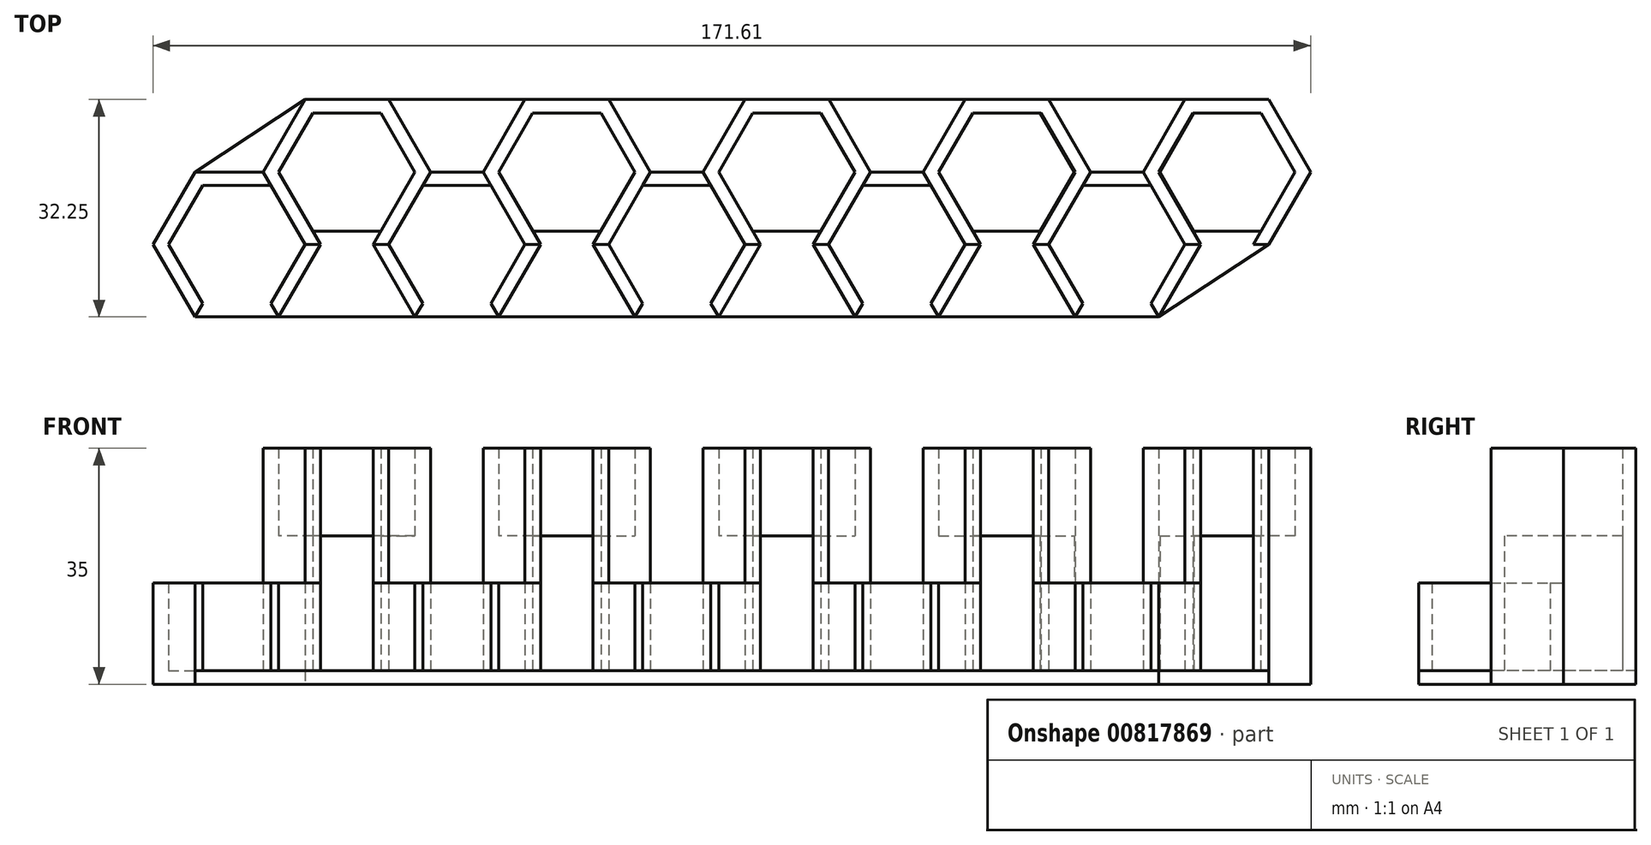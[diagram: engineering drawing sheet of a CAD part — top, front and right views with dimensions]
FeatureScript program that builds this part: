
annotation { "Feature Type Name" : "Feature", "Feature Type Description" : "" }
export const myFeature = defineFeature(function(context is Context, id is Id, definition is map)
    precondition{}
    {
        {
            var Q0;
            Q0=qCreatedBy(makeId("Top.planeOp"),FACE);
            var sketch = newSketch(context, id + "F0", { "sketchPlane" : qUnion([Q0])});
            skLineSegment(sketch, "E0.0", {"start": v(-33.3, -2) * mm, "end": v(-28.26, -10.75) * mm});
            skLineSegment(sketch, "E0.1", {"start": v(-28.26, -10.75) * mm, "end": v(-33.3, -19.5) * mm});
            skLineSegment(sketch, "E0.3", {"start": v(-43.41, -19.5) * mm, "end": v(-48.46, -10.75) * mm});
            skLineSegment(sketch, "E0.4", {"start": v(-48.46, -10.75) * mm, "end": v(-43.41, -2) * mm});
            skLineSegment(sketch, "E0.5", {"start": v(-43.41, -2) * mm, "end": v(-33.3, -2) * mm});
            skPoint(sketch, "E0.0.midPoint", {"position": v(-30.78, -6.38) * mm});
            skLineSegment(sketch, "E1.0", {"start": v(-32.15, 0) * mm, "end": v(-25.95, -10.75) * mm});
            skLineSegment(sketch, "E1.1", {"start": v(-25.95, -10.75) * mm, "end": v(-32.15, -21.5) * mm});
            skLineSegment(sketch, "E1.3", {"start": v(-44.57, -21.5) * mm, "end": v(-50.77, -10.75) * mm});
            skLineSegment(sketch, "E1.4", {"start": v(-50.77, -10.75) * mm, "end": v(-44.57, 0) * mm});
            skLineSegment(sketch, "E1.5", {"start": v(-42.26, 0) * mm, "end": v(-34.46, 0) * mm});
            skPoint(sketch, "E1.0.midPoint", {"position": v(-29.05, -5.38) * mm});
            skLineSegment(sketch, "E2.2", {"start": v(-27.1, -8.75) * mm, "end": v(-32.15, 0) * mm});
            skLineSegment(sketch, "E2.3", {"start": v(-32.15, 0) * mm, "end": v(-27.1, 8.75) * mm});
            skLineSegment(sketch, "E2.4", {"start": v(-27.1, 8.75) * mm, "end": v(-22.05, 8.75) * mm});
            skPoint(sketch, "E2.0.midPoint", {"position": v(-14.47, -4.38) * mm});
            skLineSegment(sketch, "E3.3", {"start": v(-28.26, -10.75) * mm, "end": v(-33.3, -2) * mm});
            skLineSegment(sketch, "E3.4", {"start": v(-34.46, 0) * mm, "end": v(-28.26, 10.75) * mm});
            skLineSegment(sketch, "E3.5", {"start": v(-28.26, 10.75) * mm, "end": v(-22.05, 10.75) * mm});
            skPoint(sketch, "E3.0.midPoint", {"position": v(-12.74, 5.37) * mm});
            skLineSegment(sketch, "E4", {"start": v(-44.57, -21.5) * mm, "end": v(-43.41, -19.5) * mm});
            skLineSegment(sketch, "E5", {"start": v(-33.3, -19.5) * mm, "end": v(-32.15, -21.5) * mm});
            skLineSegment(sketch, "E6", {"start": v(-22.05, 10.75) * mm, "end": v(-22.05, -27.83) * mm, "construction": true});
            skLineSegment(sketch, "E7", {"start": v(-22.05, -27.83) * mm, "end": v(-22.05, 12.83) * mm, "construction": true});
            skPoint(sketch, "E8.orphan", {"position": v(-15.84, 10.75) * mm});
            skPoint(sketch, "E3.1.start.orphan", {"position": v(-9.64, 0) * mm});
            skPoint(sketch, "E9.orphan", {"position": v(-11.95, 0) * mm});
            skPoint(sketch, "E10.end.orphan", {"position": v(-17, -8.75) * mm});
            skLineSegment(sketch, "E11.MirrorCS", {"start": v(-17, 8.75) * mm, "end": v(-22.05, 8.75) * mm});
            skLineSegment(sketch, "E12.MirrorCS", {"start": v(-15.84, 10.75) * mm, "end": v(-22.05, 10.75) * mm});
            skLineSegment(sketch, "E13.MirrorCS", {"start": v(-9.64, 0) * mm, "end": v(-15.84, 10.75) * mm});
            skLineSegment(sketch, "E14.MirrorCS", {"start": v(-11.95, 0) * mm, "end": v(-17, 8.75) * mm});
            skLineSegment(sketch, "E15.MirrorCS", {"start": v(-17, -8.75) * mm, "end": v(-11.95, 0) * mm});
            skLineSegment(sketch, "E16.MirrorCS", {"start": v(-14.47, -4.38) * mm, "end": v(-18.15, -10.75) * mm});
            skLineSegment(sketch, "E17.MirrorCS", {"start": v(-10.8, -2) * mm, "end": v(-15.84, -10.75) * mm});
            skLineSegment(sketch, "E18.1.0.0", {"start": v(-77.19, -21.5) * mm, "end": v(-83.4, -10.75) * mm});
            skLineSegment(sketch, "E18.1.0.1", {"start": v(-77.19, -21.5) * mm, "end": v(-76.03, -19.5) * mm});
            skLineSegment(sketch, "E18.1.0.2", {"start": v(-76.03, -19.5) * mm, "end": v(-81.08, -10.75) * mm});
            skLineSegment(sketch, "E18.1.0.3", {"start": v(-83.4, -10.75) * mm, "end": v(-77.19, 0) * mm});
            skLineSegment(sketch, "E18.1.0.4", {"start": v(-81.08, -10.75) * mm, "end": v(-76.03, -2) * mm});
            skLineSegment(sketch, "E18.1.0.5", {"start": v(-74.88, 0) * mm, "end": v(-67.08, 0) * mm});
            skLineSegment(sketch, "E18.1.0.6", {"start": v(-76.03, -2) * mm, "end": v(-65.93, -2) * mm});
            skLineSegment(sketch, "E18.1.0.7", {"start": v(-65.93, -2) * mm, "end": v(-60.88, -10.75) * mm});
            skLineSegment(sketch, "E18.1.0.8", {"start": v(-60.88, -10.75) * mm, "end": v(-65.93, -19.5) * mm});
            skLineSegment(sketch, "E18.1.0.9", {"start": v(-65.93, -19.5) * mm, "end": v(-64.77, -21.5) * mm});
            skLineSegment(sketch, "E18.1.0.10", {"start": v(-58.57, -10.75) * mm, "end": v(-64.77, -21.5) * mm});
            skLineSegment(sketch, "E18.1.0.11", {"start": v(-64.77, 0) * mm, "end": v(-58.57, -10.75) * mm});
            skLineSegment(sketch, "E18.1.0.12", {"start": v(-67.08, 0) * mm, "end": v(-60.88, 10.75) * mm});
            skLineSegment(sketch, "E18.1.0.13", {"start": v(-64.77, 0) * mm, "end": v(-59.72, 8.75) * mm});
            skLineSegment(sketch, "E18.1.0.14", {"start": v(-60.88, 10.75) * mm, "end": v(-54.67, 10.75) * mm});
            skLineSegment(sketch, "E18.1.0.15", {"start": v(-59.72, 8.75) * mm, "end": v(-54.67, 8.75) * mm});
            skLineSegment(sketch, "E18.1.0.16", {"start": v(-49.62, 8.75) * mm, "end": v(-54.67, 8.75) * mm});
            skLineSegment(sketch, "E18.1.0.17", {"start": v(-48.46, 10.75) * mm, "end": v(-54.67, 10.75) * mm});
            skLineSegment(sketch, "E18.1.0.18", {"start": v(-42.26, 0) * mm, "end": v(-48.46, 10.75) * mm});
            skLineSegment(sketch, "E18.1.0.19", {"start": v(-44.57, 0) * mm, "end": v(-49.62, 8.75) * mm});
            skLineSegment(sketch, "E18.2.0.0", {"start": v(-109.8, -21.5) * mm, "end": v(-116.01, -10.75) * mm});
            skLineSegment(sketch, "E18.2.0.1", {"start": v(-109.8, -21.5) * mm, "end": v(-108.65, -19.5) * mm});
            skLineSegment(sketch, "E18.2.0.2", {"start": v(-108.65, -19.5) * mm, "end": v(-113.7, -10.75) * mm});
            skLineSegment(sketch, "E18.2.0.3", {"start": v(-116.01, -10.75) * mm, "end": v(-109.8, 0) * mm});
            skLineSegment(sketch, "E18.2.0.4", {"start": v(-113.7, -10.75) * mm, "end": v(-108.65, -2) * mm});
            skLineSegment(sketch, "E18.2.0.5", {"start": v(-107.5, 0) * mm, "end": v(-99.7, 0) * mm});
            skLineSegment(sketch, "E18.2.0.6", {"start": v(-108.65, -2) * mm, "end": v(-98.55, -2) * mm});
            skLineSegment(sketch, "E18.2.0.7", {"start": v(-98.55, -2) * mm, "end": v(-93.5, -10.75) * mm});
            skLineSegment(sketch, "E18.2.0.8", {"start": v(-93.5, -10.75) * mm, "end": v(-98.55, -19.5) * mm});
            skLineSegment(sketch, "E18.2.0.9", {"start": v(-98.55, -19.5) * mm, "end": v(-97.4, -21.5) * mm});
            skLineSegment(sketch, "E18.2.0.10", {"start": v(-91.19, -10.75) * mm, "end": v(-97.4, -21.5) * mm});
            skLineSegment(sketch, "E18.2.0.11", {"start": v(-97.4, 0) * mm, "end": v(-91.19, -10.75) * mm});
            skLineSegment(sketch, "E18.2.0.12", {"start": v(-99.7, 0) * mm, "end": v(-93.5, 10.75) * mm});
            skLineSegment(sketch, "E18.2.0.13", {"start": v(-97.4, 0) * mm, "end": v(-92.34, 8.75) * mm});
            skLineSegment(sketch, "E18.2.0.14", {"start": v(-93.5, 10.75) * mm, "end": v(-87.29, 10.75) * mm});
            skLineSegment(sketch, "E18.2.0.15", {"start": v(-92.34, 8.75) * mm, "end": v(-87.29, 8.75) * mm});
            skLineSegment(sketch, "E18.2.0.16", {"start": v(-82.24, 8.75) * mm, "end": v(-87.29, 8.75) * mm});
            skLineSegment(sketch, "E18.2.0.17", {"start": v(-81.08, 10.75) * mm, "end": v(-87.29, 10.75) * mm});
            skLineSegment(sketch, "E18.2.0.18", {"start": v(-74.88, 0) * mm, "end": v(-81.08, 10.75) * mm});
            skLineSegment(sketch, "E18.2.0.19", {"start": v(-77.19, 0) * mm, "end": v(-82.24, 8.75) * mm});
            skLineSegment(sketch, "E18.3.0.0", {"start": v(-142.43, -21.5) * mm, "end": v(-148.63, -10.75) * mm});
            skLineSegment(sketch, "E18.3.0.1", {"start": v(-142.43, -21.5) * mm, "end": v(-141.27, -19.5) * mm});
            skLineSegment(sketch, "E18.3.0.2", {"start": v(-141.27, -19.5) * mm, "end": v(-146.32, -10.75) * mm});
            skLineSegment(sketch, "E18.3.0.3", {"start": v(-148.63, -10.75) * mm, "end": v(-142.43, 0) * mm});
            skLineSegment(sketch, "E18.3.0.4", {"start": v(-146.32, -10.75) * mm, "end": v(-141.27, -2) * mm});
            skLineSegment(sketch, "E18.3.0.5", {"start": v(-140.12, 0) * mm, "end": v(-132.32, 0) * mm});
            skLineSegment(sketch, "E18.3.0.6", {"start": v(-141.27, -2) * mm, "end": v(-131.17, -2) * mm});
            skLineSegment(sketch, "E18.3.0.7", {"start": v(-131.17, -2) * mm, "end": v(-126.12, -10.75) * mm});
            skLineSegment(sketch, "E18.3.0.8", {"start": v(-126.12, -10.75) * mm, "end": v(-131.17, -19.5) * mm});
            skLineSegment(sketch, "E18.3.0.9", {"start": v(-131.17, -19.5) * mm, "end": v(-130.01, -21.5) * mm});
            skLineSegment(sketch, "E18.3.0.10", {"start": v(-123.8, -10.75) * mm, "end": v(-130.01, -21.5) * mm});
            skLineSegment(sketch, "E18.3.0.11", {"start": v(-130.01, 0) * mm, "end": v(-123.8, -10.75) * mm});
            skLineSegment(sketch, "E18.3.0.12", {"start": v(-132.32, 0) * mm, "end": v(-126.12, 10.75) * mm});
            skLineSegment(sketch, "E18.3.0.13", {"start": v(-130.01, 0) * mm, "end": v(-124.96, 8.75) * mm});
            skLineSegment(sketch, "E18.3.0.14", {"start": v(-126.12, 10.75) * mm, "end": v(-119.9, 10.75) * mm});
            skLineSegment(sketch, "E18.3.0.15", {"start": v(-124.96, 8.75) * mm, "end": v(-119.9, 8.75) * mm});
            skLineSegment(sketch, "E18.3.0.16", {"start": v(-114.86, 8.75) * mm, "end": v(-119.9, 8.75) * mm});
            skLineSegment(sketch, "E18.3.0.17", {"start": v(-113.7, 10.75) * mm, "end": v(-119.9, 10.75) * mm});
            skLineSegment(sketch, "E18.3.0.18", {"start": v(-107.5, 0) * mm, "end": v(-113.7, 10.75) * mm});
            skLineSegment(sketch, "E18.3.0.19", {"start": v(-109.8, 0) * mm, "end": v(-114.86, 8.75) * mm});
            skLineSegment(sketch, "E18.4.0.0", {"start": v(-175.05, -21.5) * mm, "end": v(-181.25, -10.75) * mm});
            skLineSegment(sketch, "E18.4.0.1", {"start": v(-175.05, -21.5) * mm, "end": v(-173.9, -19.5) * mm});
            skLineSegment(sketch, "E18.4.0.2", {"start": v(-173.9, -19.5) * mm, "end": v(-178.94, -10.75) * mm});
            skLineSegment(sketch, "E18.4.0.3", {"start": v(-181.25, -10.75) * mm, "end": v(-175.05, 0) * mm});
            skLineSegment(sketch, "E18.4.0.4", {"start": v(-178.94, -10.75) * mm, "end": v(-173.9, -2) * mm});
            skLineSegment(sketch, "E18.4.0.5", {"start": v(-175.05, 0) * mm, "end": v(-164.94, 0) * mm});
            skLineSegment(sketch, "E18.4.0.6", {"start": v(-173.9, -2) * mm, "end": v(-163.79, -2) * mm});
            skLineSegment(sketch, "E18.4.0.7", {"start": v(-163.79, -2) * mm, "end": v(-158.74, -10.75) * mm});
            skLineSegment(sketch, "E18.4.0.8", {"start": v(-158.74, -10.75) * mm, "end": v(-163.79, -19.5) * mm});
            skLineSegment(sketch, "E18.4.0.9", {"start": v(-163.79, -19.5) * mm, "end": v(-162.63, -21.5) * mm});
            skLineSegment(sketch, "E18.4.0.10", {"start": v(-156.43, -10.75) * mm, "end": v(-162.63, -21.5) * mm});
            skLineSegment(sketch, "E18.4.0.11", {"start": v(-162.63, 0) * mm, "end": v(-156.43, -10.75) * mm});
            skLineSegment(sketch, "E18.4.0.12", {"start": v(-164.94, 0) * mm, "end": v(-158.74, 10.75) * mm});
            skLineSegment(sketch, "E18.4.0.13", {"start": v(-162.63, 0) * mm, "end": v(-157.58, 8.75) * mm});
            skLineSegment(sketch, "E18.4.0.14", {"start": v(-158.74, 10.75) * mm, "end": v(-152.53, 10.75) * mm});
            skLineSegment(sketch, "E18.4.0.15", {"start": v(-157.58, 8.75) * mm, "end": v(-152.53, 8.75) * mm});
            skLineSegment(sketch, "E18.4.0.16", {"start": v(-147.48, 8.75) * mm, "end": v(-152.53, 8.75) * mm});
            skLineSegment(sketch, "E18.4.0.17", {"start": v(-146.32, 10.75) * mm, "end": v(-152.53, 10.75) * mm});
            skLineSegment(sketch, "E18.4.0.18", {"start": v(-140.12, 0) * mm, "end": v(-146.32, 10.75) * mm});
            skLineSegment(sketch, "E18.4.0.19", {"start": v(-142.43, 0) * mm, "end": v(-147.48, 8.75) * mm});
            skLineSegment(sketch, "E18.direction1", {"start": v(-44.57, -21.5) * mm, "end": v(-77.19, -21.5) * mm, "construction": true});
            skPoint(sketch, "E19.MirrorCS.end.orphan", {"position": v(-10.8, -19.5) * mm});
            skPoint(sketch, "E19.MirrorCS.start.orphan", {"position": v(-15.84, -10.75) * mm});
            skPoint(sketch, "E20.MirrorCS.end.orphan", {"position": v(-11.95, -21.5) * mm});
            skPoint(sketch, "E20.MirrorCS.start.orphan", {"position": v(-18.15, -10.75) * mm});
            skPoint(sketch, "E21.MirrorCS.end.orphan", {"position": v(-0.69, -19.5) * mm});
            skPoint(sketch, "E21.MirrorCS.start.orphan", {"position": v(0.47, -21.5) * mm});
            skPoint(sketch, "E22.MirrorCS.end.orphan", {"position": v(4.36, -10.75) * mm});
            skPoint(sketch, "E23.MirrorCS.end.orphan", {"position": v(6.67, -10.75) * mm});
            skPoint(sketch, "E24.MirrorCS.end.orphan", {"position": v(-0.69, -2) * mm});
            skPoint(sketch, "E25.MirrorCS.end.orphan", {"position": v(0.47, 0) * mm});
            skPoint(sketch, "E26.MirrorCS.end.orphan", {"position": v(-10.8, -2) * mm});
            skLineSegment(sketch, "E27", {"start": v(-10.8, -2) * mm, "end": v(-9.64, 0) * mm});
            skLineSegment(sketch, "E28", {"start": v(-15.84, -10.75) * mm, "end": v(-18.15, -10.75) * mm});
            skLineSegment(sketch, "E29", {"start": v(-77.19, 0) * mm, "end": v(-83.4, -10.75) * mm});
            skLineSegment(sketch, "E30", {"start": v(-109.8, 0) * mm, "end": v(-116.01, -10.75) * mm});
            skSolve(sketch);
        }
        {
            var Q0;
            Q0 = qSketchRegion(id + "F0", true);
            extrude(context, id + "F1", {"entities" : qUnion([Q0]), "depth" : 15 * mm, "offsetDistance" : 25 * mm});
        }
        {
            var Q0;
            Q0=makeQuery(id+"F1.opExtrude","CAP_FACE",FACE,{"disambiguationData":[OSD([sQuery(id+"F0.wireOp",EDGE,"E0.1"),sQuery(id+"F0.wireOp",EDGE,"E0.3"),sQuery(id+"F0.wireOp",EDGE,"E0.4"),sQuery(id+"F0.wireOp",EDGE,"E0.5"),sQuery(id+"F0.wireOp",EDGE,"E1.0"),sQuery(id+"F0.wireOp",EDGE,"E1.1"),sQuery(id+"F0.wireOp",EDGE,"E1.3"),sQuery(id+"F0.wireOp",EDGE,"E1.5"),sQuery(id+"F0.wireOp",EDGE,"E2.2"),sQuery(id+"F0.wireOp",EDGE,"E2.3"),sQuery(id+"F0.wireOp",EDGE,"E2.4"),sQuery(id+"F0.wireOp",EDGE,"E3.3"),sQuery(id+"F0.wireOp",EDGE,"E3.4"),sQuery(id+"F0.wireOp",EDGE,"E3.5"),sQuery(id+"F0.wireOp",EDGE,"E4"),sQuery(id+"F0.wireOp",EDGE,"E5"),sQuery(id+"F0.wireOp",EDGE,"E11.MirrorCS"),sQuery(id+"F0.wireOp",EDGE,"E12.MirrorCS"),sQuery(id+"F0.wireOp",EDGE,"E13.MirrorCS"),sQuery(id+"F0.wireOp",EDGE,"E14.MirrorCS"),sQuery(id+"F0.wireOp",EDGE,"E15.MirrorCS"),sQuery(id+"F0.wireOp",EDGE,"E16.MirrorCS"),sQuery(id+"F0.wireOp",EDGE,"E17.MirrorCS"),sQuery(id+"F0.wireOp",EDGE,"E18.1.0.0"),sQuery(id+"F0.wireOp",EDGE,"E18.1.0.1"),sQuery(id+"F0.wireOp",EDGE,"E18.1.0.2"),sQuery(id+"F0.wireOp",EDGE,"E18.1.0.4"),sQuery(id+"F0.wireOp",EDGE,"E18.1.0.5"),sQuery(id+"F0.wireOp",EDGE,"E18.1.0.6"),sQuery(id+"F0.wireOp",EDGE,"E18.1.0.7"),sQuery(id+"F0.wireOp",EDGE,"E18.1.0.8"),sQuery(id+"F0.wireOp",EDGE,"E18.1.0.9"),sQuery(id+"F0.wireOp",EDGE,"E18.1.0.10"),sQuery(id+"F0.wireOp",EDGE,"E18.1.0.11"),sQuery(id+"F0.wireOp",EDGE,"E18.1.0.12"),sQuery(id+"F0.wireOp",EDGE,"E18.1.0.13"),sQuery(id+"F0.wireOp",EDGE,"E18.1.0.14"),sQuery(id+"F0.wireOp",EDGE,"E18.1.0.15"),sQuery(id+"F0.wireOp",EDGE,"E18.1.0.16"),sQuery(id+"F0.wireOp",EDGE,"E18.1.0.17"),sQuery(id+"F0.wireOp",EDGE,"E18.1.0.18"),sQuery(id+"F0.wireOp",EDGE,"E18.1.0.19"),sQuery(id+"F0.wireOp",EDGE,"E18.2.0.0"),sQuery(id+"F0.wireOp",EDGE,"E18.2.0.1"),sQuery(id+"F0.wireOp",EDGE,"E18.2.0.2"),sQuery(id+"F0.wireOp",EDGE,"E18.2.0.4"),sQuery(id+"F0.wireOp",EDGE,"E18.2.0.5"),sQuery(id+"F0.wireOp",EDGE,"E18.2.0.6"),sQuery(id+"F0.wireOp",EDGE,"E18.2.0.7"),sQuery(id+"F0.wireOp",EDGE,"E18.2.0.8"),sQuery(id+"F0.wireOp",EDGE,"E18.2.0.9"),sQuery(id+"F0.wireOp",EDGE,"E18.2.0.10"),sQuery(id+"F0.wireOp",EDGE,"E18.2.0.11"),sQuery(id+"F0.wireOp",EDGE,"E18.2.0.12"),sQuery(id+"F0.wireOp",EDGE,"E18.2.0.13"),sQuery(id+"F0.wireOp",EDGE,"E18.2.0.14"),sQuery(id+"F0.wireOp",EDGE,"E18.2.0.15"),sQuery(id+"F0.wireOp",EDGE,"E18.2.0.16"),sQuery(id+"F0.wireOp",EDGE,"E18.2.0.17"),sQuery(id+"F0.wireOp",EDGE,"E18.2.0.18"),sQuery(id+"F0.wireOp",EDGE,"E18.2.0.19"),sQuery(id+"F0.wireOp",EDGE,"E18.3.0.0"),sQuery(id+"F0.wireOp",EDGE,"E18.3.0.1"),sQuery(id+"F0.wireOp",EDGE,"E18.3.0.2"),sQuery(id+"F0.wireOp",EDGE,"E18.3.0.4"),sQuery(id+"F0.wireOp",EDGE,"E18.3.0.5"),sQuery(id+"F0.wireOp",EDGE,"E18.3.0.6"),sQuery(id+"F0.wireOp",EDGE,"E18.3.0.7"),sQuery(id+"F0.wireOp",EDGE,"E18.3.0.8"),sQuery(id+"F0.wireOp",EDGE,"E18.3.0.9"),sQuery(id+"F0.wireOp",EDGE,"E18.3.0.10"),sQuery(id+"F0.wireOp",EDGE,"E18.3.0.11"),sQuery(id+"F0.wireOp",EDGE,"E18.3.0.12"),sQuery(id+"F0.wireOp",EDGE,"E18.3.0.13"),sQuery(id+"F0.wireOp",EDGE,"E18.3.0.14"),sQuery(id+"F0.wireOp",EDGE,"E18.3.0.15"),sQuery(id+"F0.wireOp",EDGE,"E18.3.0.16"),sQuery(id+"F0.wireOp",EDGE,"E18.3.0.17"),sQuery(id+"F0.wireOp",EDGE,"E18.3.0.18"),sQuery(id+"F0.wireOp",EDGE,"E18.3.0.19"),sQuery(id+"F0.wireOp",EDGE,"E18.4.0.0"),sQuery(id+"F0.wireOp",EDGE,"E18.4.0.1"),sQuery(id+"F0.wireOp",EDGE,"E18.4.0.2"),sQuery(id+"F0.wireOp",EDGE,"E18.4.0.3"),sQuery(id+"F0.wireOp",EDGE,"E18.4.0.4"),sQuery(id+"F0.wireOp",EDGE,"E18.4.0.5"),sQuery(id+"F0.wireOp",EDGE,"E18.4.0.6"),sQuery(id+"F0.wireOp",EDGE,"E18.4.0.7"),sQuery(id+"F0.wireOp",EDGE,"E18.4.0.8"),sQuery(id+"F0.wireOp",EDGE,"E18.4.0.9"),sQuery(id+"F0.wireOp",EDGE,"E18.4.0.10"),sQuery(id+"F0.wireOp",EDGE,"E18.4.0.11"),sQuery(id+"F0.wireOp",EDGE,"E18.4.0.12"),sQuery(id+"F0.wireOp",EDGE,"E18.4.0.13"),sQuery(id+"F0.wireOp",EDGE,"E18.4.0.14"),sQuery(id+"F0.wireOp",EDGE,"E18.4.0.15"),sQuery(id+"F0.wireOp",EDGE,"E18.4.0.16"),sQuery(id+"F0.wireOp",EDGE,"E18.4.0.17"),sQuery(id+"F0.wireOp",EDGE,"E18.4.0.18"),sQuery(id+"F0.wireOp",EDGE,"E18.4.0.19"),sQuery(id+"F0.wireOp",EDGE,"E27"),sQuery(id+"F0.wireOp",EDGE,"E28"),sQuery(id+"F0.wireOp",EDGE,"E1.4"),sQuery(id+"F0.wireOp",EDGE,"E29"),sQuery(id+"F0.wireOp",EDGE,"E30"),sQuery(id+"F0.wireOp",EDGE,"E18.3.0.3")])],"isStart":true});
            var sketch = newSketch(context, id + "F2", { "sketchPlane" : qUnion([Q0])});
            skLineSegment(sketch, "E31", {"start": v(-175.05, 21.5) * mm, "end": v(-32.15, 21.5) * mm});
            skLineSegment(sketch, "E32", {"start": v(-32.15, 21.5) * mm, "end": v(-15.84, 10.75) * mm});
            skLineSegment(sketch, "E33", {"start": v(-15.84, 10.75) * mm, "end": v(-9.64, 0) * mm});
            skLineSegment(sketch, "E34", {"start": v(-9.64, 0) * mm, "end": v(-15.84, -10.75) * mm});
            skLineSegment(sketch, "E35", {"start": v(-15.84, -10.75) * mm, "end": v(-158.74, -10.75) * mm});
            skLineSegment(sketch, "E36", {"start": v(-158.74, -10.75) * mm, "end": v(-175.05, 0) * mm});
            skLineSegment(sketch, "E37", {"start": v(-175.05, 0) * mm, "end": v(-181.25, 10.75) * mm});
            skLineSegment(sketch, "E38", {"start": v(-181.25, 10.75) * mm, "end": v(-175.05, 21.5) * mm});
            skSolve(sketch);
        }
        {
            var Q0;
            Q0 = qSketchRegion(id + "F2", true);
            extrude(context, id + "F3", {"entities" : qUnion([Q0]), "operationType" : NewBodyOperationType.ADD, "oppositeDirection" : true, "depth" : 2 * mm, "offsetDistance" : 25 * mm});
        }
        {
            var Q0;
            Q0=makeQuery(id+"F1.opExtrude","CAP_FACE",FACE,{"disambiguationData":[OSD([sQuery(id+"F0.wireOp",EDGE,"E0.1"),sQuery(id+"F0.wireOp",EDGE,"E0.3"),sQuery(id+"F0.wireOp",EDGE,"E0.4"),sQuery(id+"F0.wireOp",EDGE,"E0.5"),sQuery(id+"F0.wireOp",EDGE,"E1.0"),sQuery(id+"F0.wireOp",EDGE,"E1.1"),sQuery(id+"F0.wireOp",EDGE,"E1.3"),sQuery(id+"F0.wireOp",EDGE,"E1.5"),sQuery(id+"F0.wireOp",EDGE,"E2.2"),sQuery(id+"F0.wireOp",EDGE,"E2.3"),sQuery(id+"F0.wireOp",EDGE,"E2.4"),sQuery(id+"F0.wireOp",EDGE,"E3.3"),sQuery(id+"F0.wireOp",EDGE,"E3.4"),sQuery(id+"F0.wireOp",EDGE,"E3.5"),sQuery(id+"F0.wireOp",EDGE,"E4"),sQuery(id+"F0.wireOp",EDGE,"E5"),sQuery(id+"F0.wireOp",EDGE,"E11.MirrorCS"),sQuery(id+"F0.wireOp",EDGE,"E12.MirrorCS"),sQuery(id+"F0.wireOp",EDGE,"E13.MirrorCS"),sQuery(id+"F0.wireOp",EDGE,"E14.MirrorCS"),sQuery(id+"F0.wireOp",EDGE,"E15.MirrorCS"),sQuery(id+"F0.wireOp",EDGE,"E16.MirrorCS"),sQuery(id+"F0.wireOp",EDGE,"E17.MirrorCS"),sQuery(id+"F0.wireOp",EDGE,"E18.1.0.0"),sQuery(id+"F0.wireOp",EDGE,"E18.1.0.1"),sQuery(id+"F0.wireOp",EDGE,"E18.1.0.2"),sQuery(id+"F0.wireOp",EDGE,"E18.1.0.4"),sQuery(id+"F0.wireOp",EDGE,"E18.1.0.5"),sQuery(id+"F0.wireOp",EDGE,"E18.1.0.6"),sQuery(id+"F0.wireOp",EDGE,"E18.1.0.7"),sQuery(id+"F0.wireOp",EDGE,"E18.1.0.8"),sQuery(id+"F0.wireOp",EDGE,"E18.1.0.9"),sQuery(id+"F0.wireOp",EDGE,"E18.1.0.10"),sQuery(id+"F0.wireOp",EDGE,"E18.1.0.11"),sQuery(id+"F0.wireOp",EDGE,"E18.1.0.12"),sQuery(id+"F0.wireOp",EDGE,"E18.1.0.13"),sQuery(id+"F0.wireOp",EDGE,"E18.1.0.14"),sQuery(id+"F0.wireOp",EDGE,"E18.1.0.15"),sQuery(id+"F0.wireOp",EDGE,"E18.1.0.16"),sQuery(id+"F0.wireOp",EDGE,"E18.1.0.17"),sQuery(id+"F0.wireOp",EDGE,"E18.1.0.18"),sQuery(id+"F0.wireOp",EDGE,"E18.1.0.19"),sQuery(id+"F0.wireOp",EDGE,"E18.2.0.0"),sQuery(id+"F0.wireOp",EDGE,"E18.2.0.1"),sQuery(id+"F0.wireOp",EDGE,"E18.2.0.2"),sQuery(id+"F0.wireOp",EDGE,"E18.2.0.4"),sQuery(id+"F0.wireOp",EDGE,"E18.2.0.5"),sQuery(id+"F0.wireOp",EDGE,"E18.2.0.6"),sQuery(id+"F0.wireOp",EDGE,"E18.2.0.7"),sQuery(id+"F0.wireOp",EDGE,"E18.2.0.8"),sQuery(id+"F0.wireOp",EDGE,"E18.2.0.9"),sQuery(id+"F0.wireOp",EDGE,"E18.2.0.10"),sQuery(id+"F0.wireOp",EDGE,"E18.2.0.11"),sQuery(id+"F0.wireOp",EDGE,"E18.2.0.12"),sQuery(id+"F0.wireOp",EDGE,"E18.2.0.13"),sQuery(id+"F0.wireOp",EDGE,"E18.2.0.14"),sQuery(id+"F0.wireOp",EDGE,"E18.2.0.15"),sQuery(id+"F0.wireOp",EDGE,"E18.2.0.16"),sQuery(id+"F0.wireOp",EDGE,"E18.2.0.17"),sQuery(id+"F0.wireOp",EDGE,"E18.2.0.18"),sQuery(id+"F0.wireOp",EDGE,"E18.2.0.19"),sQuery(id+"F0.wireOp",EDGE,"E18.3.0.0"),sQuery(id+"F0.wireOp",EDGE,"E18.3.0.1"),sQuery(id+"F0.wireOp",EDGE,"E18.3.0.2"),sQuery(id+"F0.wireOp",EDGE,"E18.3.0.4"),sQuery(id+"F0.wireOp",EDGE,"E18.3.0.5"),sQuery(id+"F0.wireOp",EDGE,"E18.3.0.6"),sQuery(id+"F0.wireOp",EDGE,"E18.3.0.7"),sQuery(id+"F0.wireOp",EDGE,"E18.3.0.8"),sQuery(id+"F0.wireOp",EDGE,"E18.3.0.9"),sQuery(id+"F0.wireOp",EDGE,"E18.3.0.10"),sQuery(id+"F0.wireOp",EDGE,"E18.3.0.11"),sQuery(id+"F0.wireOp",EDGE,"E18.3.0.12"),sQuery(id+"F0.wireOp",EDGE,"E18.3.0.13"),sQuery(id+"F0.wireOp",EDGE,"E18.3.0.14"),sQuery(id+"F0.wireOp",EDGE,"E18.3.0.15"),sQuery(id+"F0.wireOp",EDGE,"E18.3.0.16"),sQuery(id+"F0.wireOp",EDGE,"E18.3.0.17"),sQuery(id+"F0.wireOp",EDGE,"E18.3.0.18"),sQuery(id+"F0.wireOp",EDGE,"E18.3.0.19"),sQuery(id+"F0.wireOp",EDGE,"E18.4.0.0"),sQuery(id+"F0.wireOp",EDGE,"E18.4.0.1"),sQuery(id+"F0.wireOp",EDGE,"E18.4.0.2"),sQuery(id+"F0.wireOp",EDGE,"E18.4.0.3"),sQuery(id+"F0.wireOp",EDGE,"E18.4.0.4"),sQuery(id+"F0.wireOp",EDGE,"E18.4.0.5"),sQuery(id+"F0.wireOp",EDGE,"E18.4.0.6"),sQuery(id+"F0.wireOp",EDGE,"E18.4.0.7"),sQuery(id+"F0.wireOp",EDGE,"E18.4.0.8"),sQuery(id+"F0.wireOp",EDGE,"E18.4.0.9"),sQuery(id+"F0.wireOp",EDGE,"E18.4.0.10"),sQuery(id+"F0.wireOp",EDGE,"E18.4.0.11"),sQuery(id+"F0.wireOp",EDGE,"E18.4.0.12"),sQuery(id+"F0.wireOp",EDGE,"E18.4.0.13"),sQuery(id+"F0.wireOp",EDGE,"E18.4.0.14"),sQuery(id+"F0.wireOp",EDGE,"E18.4.0.15"),sQuery(id+"F0.wireOp",EDGE,"E18.4.0.16"),sQuery(id+"F0.wireOp",EDGE,"E18.4.0.17"),sQuery(id+"F0.wireOp",EDGE,"E18.4.0.18"),sQuery(id+"F0.wireOp",EDGE,"E18.4.0.19"),sQuery(id+"F0.wireOp",EDGE,"E27"),sQuery(id+"F0.wireOp",EDGE,"E28"),sQuery(id+"F0.wireOp",EDGE,"E1.4"),sQuery(id+"F0.wireOp",EDGE,"E29"),sQuery(id+"F0.wireOp",EDGE,"E30"),sQuery(id+"F0.wireOp",EDGE,"E18.3.0.3")])],"isStart":false});
            var sketch = newSketch(context, id + "F4", { "sketchPlane" : qUnion([Q0])});
            skLineSegment(sketch, "E39", {"start": v(-18.15, -10.75) * mm, "end": v(-15.84, -10.75) * mm});
            skLineSegment(sketch, "E40", {"start": v(-15.84, -10.75) * mm, "end": v(-9.64, 0) * mm});
            skLineSegment(sketch, "E41", {"start": v(-9.64, 0) * mm, "end": v(-15.84, 10.75) * mm});
            skLineSegment(sketch, "E42", {"start": v(-15.84, 10.75) * mm, "end": v(-28.26, 10.75) * mm});
            skLineSegment(sketch, "E43", {"start": v(-28.26, 10.75) * mm, "end": v(-34.46, 0) * mm});
            skLineSegment(sketch, "E44", {"start": v(-42.26, 0) * mm, "end": v(-48.46, 10.75) * mm});
            skLineSegment(sketch, "E45", {"start": v(-48.46, 10.75) * mm, "end": v(-60.88, 10.75) * mm});
            skLineSegment(sketch, "E46", {"start": v(-60.88, 10.75) * mm, "end": v(-67.08, 0) * mm});
            skLineSegment(sketch, "E47", {"start": v(-74.88, 0) * mm, "end": v(-81.08, 10.75) * mm});
            skLineSegment(sketch, "E48", {"start": v(-81.08, 10.75) * mm, "end": v(-93.5, 10.75) * mm});
            skLineSegment(sketch, "E49", {"start": v(-93.5, 10.75) * mm, "end": v(-99.7, 0) * mm});
            skLineSegment(sketch, "E50", {"start": v(-107.5, 0) * mm, "end": v(-113.7, 10.75) * mm});
            skLineSegment(sketch, "E51", {"start": v(-113.7, 10.75) * mm, "end": v(-126.12, 10.75) * mm});
            skLineSegment(sketch, "E52", {"start": v(-126.12, 10.75) * mm, "end": v(-132.32, 0) * mm});
            skLineSegment(sketch, "E53", {"start": v(-140.12, 0) * mm, "end": v(-146.32, 10.75) * mm});
            skLineSegment(sketch, "E54", {"start": v(-146.32, 10.75) * mm, "end": v(-158.74, 10.75) * mm});
            skLineSegment(sketch, "E55", {"start": v(-158.74, 10.75) * mm, "end": v(-164.94, 0) * mm});
            skLineSegment(sketch, "E56", {"start": v(-164.94, 0) * mm, "end": v(-158.74, -10.75) * mm});
            skLineSegment(sketch, "E57", {"start": v(-158.74, -10.75) * mm, "end": v(-156.43, -10.75) * mm});
            skLineSegment(sketch, "E58", {"start": v(-156.43, -10.75) * mm, "end": v(-162.63, 0) * mm});
            skLineSegment(sketch, "E59", {"start": v(-162.63, 0) * mm, "end": v(-157.58, 8.75) * mm});
            skLineSegment(sketch, "E60", {"start": v(-157.58, 8.75) * mm, "end": v(-147.48, 8.75) * mm});
            skLineSegment(sketch, "E61", {"start": v(-147.48, 8.75) * mm, "end": v(-142.43, 0) * mm});
            skLineSegment(sketch, "E62", {"start": v(-142.43, 0) * mm, "end": v(-148.63, -10.75) * mm});
            skLineSegment(sketch, "E63", {"start": v(-148.63, -10.75) * mm, "end": v(-146.32, -10.75) * mm});
            skLineSegment(sketch, "E64", {"start": v(-146.32, -10.75) * mm, "end": v(-141.27, -2) * mm});
            skLineSegment(sketch, "E65", {"start": v(-141.27, -2) * mm, "end": v(-140.12, 0) * mm});
            skLineSegment(sketch, "E66", {"start": v(-132.32, 0) * mm, "end": v(-131.17, -2) * mm});
            skLineSegment(sketch, "E67", {"start": v(-131.17, -2) * mm, "end": v(-126.12, -10.75) * mm});
            skLineSegment(sketch, "E68", {"start": v(-126.12, -10.75) * mm, "end": v(-123.8, -10.75) * mm});
            skLineSegment(sketch, "E69", {"start": v(-123.8, -10.75) * mm, "end": v(-130.01, 0) * mm});
            skLineSegment(sketch, "E70", {"start": v(-130.01, 0) * mm, "end": v(-124.96, 8.75) * mm});
            skLineSegment(sketch, "E71", {"start": v(-124.96, 8.75) * mm, "end": v(-114.86, 8.75) * mm});
            skLineSegment(sketch, "E72", {"start": v(-114.86, 8.75) * mm, "end": v(-109.8, 0) * mm});
            skLineSegment(sketch, "E73", {"start": v(-109.8, 0) * mm, "end": v(-116.01, -10.75) * mm});
            skLineSegment(sketch, "E74", {"start": v(-116.01, -10.75) * mm, "end": v(-113.7, -10.75) * mm});
            skLineSegment(sketch, "E75", {"start": v(-113.7, -10.75) * mm, "end": v(-108.65, -2) * mm});
            skLineSegment(sketch, "E76", {"start": v(-108.65, -2) * mm, "end": v(-107.5, 0) * mm});
            skLineSegment(sketch, "E77", {"start": v(-99.7, 0) * mm, "end": v(-98.55, -2) * mm});
            skLineSegment(sketch, "E78", {"start": v(-98.55, -2) * mm, "end": v(-93.5, -10.75) * mm});
            skLineSegment(sketch, "E79", {"start": v(-93.5, -10.75) * mm, "end": v(-91.19, -10.75) * mm});
            skLineSegment(sketch, "E80", {"start": v(-91.19, -10.75) * mm, "end": v(-97.4, 0) * mm});
            skLineSegment(sketch, "E81", {"start": v(-97.4, 0) * mm, "end": v(-92.34, 8.75) * mm});
            skLineSegment(sketch, "E82", {"start": v(-92.34, 8.75) * mm, "end": v(-82.24, 8.75) * mm});
            skLineSegment(sketch, "E83", {"start": v(-82.24, 8.75) * mm, "end": v(-77.19, 0) * mm});
            skLineSegment(sketch, "E84", {"start": v(-77.19, 0) * mm, "end": v(-83.4, -10.75) * mm});
            skLineSegment(sketch, "E85", {"start": v(-83.4, -10.75) * mm, "end": v(-81.08, -10.75) * mm});
            skLineSegment(sketch, "E86", {"start": v(-81.08, -10.75) * mm, "end": v(-76.03, -2) * mm});
            skLineSegment(sketch, "E87", {"start": v(-76.03, -2) * mm, "end": v(-74.88, 0) * mm});
            skLineSegment(sketch, "E88", {"start": v(-67.08, 0) * mm, "end": v(-65.93, -2) * mm});
            skLineSegment(sketch, "E89", {"start": v(-65.93, -2) * mm, "end": v(-60.88, -10.75) * mm});
            skLineSegment(sketch, "E90", {"start": v(-60.88, -10.75) * mm, "end": v(-58.57, -10.75) * mm});
            skLineSegment(sketch, "E91", {"start": v(-58.57, -10.75) * mm, "end": v(-64.77, 0) * mm});
            skLineSegment(sketch, "E92", {"start": v(-64.77, 0) * mm, "end": v(-59.72, 8.75) * mm});
            skLineSegment(sketch, "E93", {"start": v(-59.72, 8.75) * mm, "end": v(-49.62, 8.75) * mm});
            skLineSegment(sketch, "E94", {"start": v(-49.62, 8.75) * mm, "end": v(-44.57, 0) * mm});
            skLineSegment(sketch, "E95", {"start": v(-44.57, 0) * mm, "end": v(-50.77, -10.75) * mm});
            skLineSegment(sketch, "E96", {"start": v(-50.77, -10.75) * mm, "end": v(-48.46, -10.75) * mm});
            skLineSegment(sketch, "E97", {"start": v(-48.46, -10.75) * mm, "end": v(-43.41, -2) * mm});
            skLineSegment(sketch, "E98", {"start": v(-43.41, -2) * mm, "end": v(-42.26, 0) * mm});
            skLineSegment(sketch, "E99", {"start": v(-34.46, 0) * mm, "end": v(-33.3, -2) * mm});
            skLineSegment(sketch, "E100", {"start": v(-33.3, -2) * mm, "end": v(-28.26, -10.75) * mm});
            skLineSegment(sketch, "E101", {"start": v(-28.26, -10.75) * mm, "end": v(-25.95, -10.75) * mm});
            skLineSegment(sketch, "E102", {"start": v(-25.95, -10.75) * mm, "end": v(-32.15, 0) * mm});
            skLineSegment(sketch, "E103", {"start": v(-32.15, 0) * mm, "end": v(-27.1, 8.75) * mm});
            skLineSegment(sketch, "E104", {"start": v(-27.1, 8.75) * mm, "end": v(-17, 8.75) * mm});
            skLineSegment(sketch, "E105", {"start": v(-17, 8.75) * mm, "end": v(-11.95, 0) * mm});
            skLineSegment(sketch, "E106", {"start": v(-11.95, 0) * mm, "end": v(-18.15, -10.75) * mm});
            skSolve(sketch);
        }
        {
            var Q0;
            Q0 = qSketchRegion(id + "F4", true);
            extrude(context, id + "F5", {"entities" : qUnion([Q0]), "operationType" : NewBodyOperationType.ADD, "depth" : 20 * mm, "offsetDistance" : 25 * mm});
        }
        {
            var Q0;
            {var subQ0=sQuery(id+"F2.wireOp",EDGE,"E31");var subQ1=makeQuery(id+"F3.opExtrude","CAP_FACE",FACE,{"disambiguationData":[OSD([subQ0,sQuery(id+"F2.wireOp",EDGE,"E32"),sQuery(id+"F2.wireOp",EDGE,"E33"),sQuery(id+"F2.wireOp",EDGE,"E34"),sQuery(id+"F2.wireOp",EDGE,"E35"),sQuery(id+"F2.wireOp",EDGE,"E36"),sQuery(id+"F2.wireOp",EDGE,"E37"),sQuery(id+"F2.wireOp",EDGE,"E38")])],"isStart":false});Q0=makeQuery(id+"F3.boolean.opBoolean","SPLIT",FACE,{"disambiguationData":[TD([makeQuery(id+"F1.opExtrude","SWEPT_FACE",FACE,{"disambiguationData":[OSD([sQuery(id+"F0.wireOp",EDGE,"E18.4.0.11")])]})])],"derivedFrom":subQ1});}
            var sketch = newSketch(context, id + "F6", { "sketchPlane" : qUnion([Q0])});
            skCircle(sketch, "E107.cCircle", {"center": v(-152.53, 0) * mm, "radius": 8.75 * mm, "construction": true});
            skPoint(sketch, "E107.cCircle.centerSnap0", {"position": v(-152.53, 8.75) * mm});
            skLineSegment(sketch, "E107.0", {"start": v(-157.58, 8.75) * mm, "end": v(-147.48, 8.75) * mm});
            skLineSegment(sketch, "E107.1", {"start": v(-147.48, 8.75) * mm, "end": v(-142.43, 0) * mm});
            skLineSegment(sketch, "E107.2", {"start": v(-142.43, 0) * mm, "end": v(-147.48, -8.75) * mm});
            skLineSegment(sketch, "E107.3", {"start": v(-147.48, -8.75) * mm, "end": v(-157.58, -8.75) * mm});
            skLineSegment(sketch, "E107.4", {"start": v(-157.58, -8.75) * mm, "end": v(-162.63, 0) * mm});
            skLineSegment(sketch, "E107.5", {"start": v(-162.63, 0) * mm, "end": v(-157.58, 8.75) * mm});
            skPoint(sketch, "E107.0.midPoint", {"position": v(-152.53, 8.75) * mm});
            skCircle(sketch, "E108.cCircle", {"center": v(-119.9, 0) * mm, "radius": 8.75 * mm, "construction": true});
            skLineSegment(sketch, "E108.0", {"start": v(-124.96, 8.75) * mm, "end": v(-114.86, 8.75) * mm});
            skLineSegment(sketch, "E108.1", {"start": v(-114.86, 8.75) * mm, "end": v(-109.8, 0) * mm});
            skLineSegment(sketch, "E108.2", {"start": v(-109.8, 0) * mm, "end": v(-114.86, -8.75) * mm});
            skLineSegment(sketch, "E108.3", {"start": v(-114.86, -8.75) * mm, "end": v(-124.96, -8.75) * mm});
            skLineSegment(sketch, "E108.4", {"start": v(-124.96, -8.75) * mm, "end": v(-130.01, 0) * mm});
            skLineSegment(sketch, "E108.5", {"start": v(-130.01, 0) * mm, "end": v(-124.96, 8.75) * mm});
            skPoint(sketch, "E108.0.midPoint", {"position": v(-119.9, 8.75) * mm});
            skCircle(sketch, "E109.cCircle", {"center": v(-87.29, 0) * mm, "radius": 8.75 * mm, "construction": true});
            skLineSegment(sketch, "E109.0", {"start": v(-92.34, 8.75) * mm, "end": v(-82.24, 8.75) * mm});
            skLineSegment(sketch, "E109.1", {"start": v(-82.24, 8.75) * mm, "end": v(-77.19, 0) * mm});
            skLineSegment(sketch, "E109.2", {"start": v(-77.19, 0) * mm, "end": v(-82.24, -8.75) * mm});
            skLineSegment(sketch, "E109.3", {"start": v(-82.24, -8.75) * mm, "end": v(-92.34, -8.75) * mm});
            skLineSegment(sketch, "E109.4", {"start": v(-92.34, -8.75) * mm, "end": v(-97.4, 0) * mm});
            skLineSegment(sketch, "E109.5", {"start": v(-97.4, 0) * mm, "end": v(-92.34, 8.75) * mm});
            skPoint(sketch, "E109.0.midPoint", {"position": v(-87.29, 8.75) * mm});
            skCircle(sketch, "E110.cCircle", {"center": v(-54.79, 0) * mm, "radius": 8.75 * mm, "construction": true});
            skLineSegment(sketch, "E110.0", {"start": v(-49.73, 8.75) * mm, "end": v(-44.68, 0) * mm});
            skLineSegment(sketch, "E110.1", {"start": v(-44.68, 0) * mm, "end": v(-49.73, -8.75) * mm});
            skLineSegment(sketch, "E110.2", {"start": v(-49.73, -8.75) * mm, "end": v(-59.84, -8.75) * mm});
            skLineSegment(sketch, "E110.3", {"start": v(-59.84, -8.75) * mm, "end": v(-64.9, 0) * mm});
            skLineSegment(sketch, "E110.4", {"start": v(-64.9, 0) * mm, "end": v(-59.84, 8.75) * mm});
            skLineSegment(sketch, "E110.5", {"start": v(-59.84, 8.75) * mm, "end": v(-49.73, 8.75) * mm});
            skPoint(sketch, "E110.0.midPoint", {"position": v(-47.2, 4.37) * mm});
            skCircle(sketch, "E111.cCircle", {"center": v(-21.88, 0) * mm, "radius": 8.75 * mm, "construction": true});
            skLineSegment(sketch, "E111.0", {"start": v(-26.93, 8.75) * mm, "end": v(-16.83, 8.75) * mm});
            skLineSegment(sketch, "E111.1", {"start": v(-16.83, 8.75) * mm, "end": v(-11.78, 0) * mm});
            skLineSegment(sketch, "E111.2", {"start": v(-11.78, 0) * mm, "end": v(-16.83, -8.75) * mm});
            skLineSegment(sketch, "E111.3", {"start": v(-16.83, -8.75) * mm, "end": v(-26.93, -8.75) * mm});
            skLineSegment(sketch, "E111.4", {"start": v(-26.93, -8.75) * mm, "end": v(-31.98, 0) * mm});
            skLineSegment(sketch, "E111.5", {"start": v(-31.98, 0) * mm, "end": v(-26.93, 8.75) * mm});
            skPoint(sketch, "E111.0.midPoint", {"position": v(-21.88, 8.75) * mm});
            skSolve(sketch);
        }
        {
            var Q0;
            Q0 = qSketchRegion(id + "F6", true);
            extrude(context, id + "F7", {"entities" : qUnion([Q0]), "operationType" : NewBodyOperationType.ADD, "depth" : 20 * mm, "offsetDistance" : 25 * mm});
        }
    });
